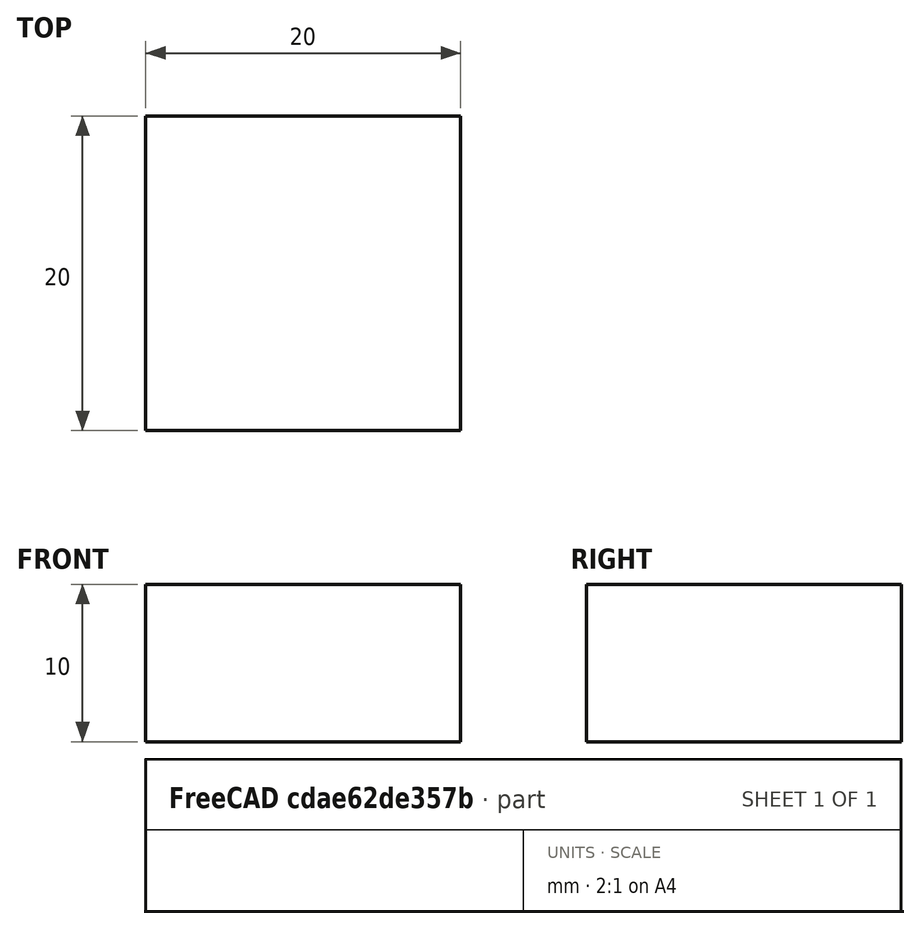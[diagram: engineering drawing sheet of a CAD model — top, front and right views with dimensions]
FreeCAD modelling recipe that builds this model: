
FCSTD DOCUMENT  (FreeCAD 1.0R39319 (Git))
Label: PD_PadWithMidplaneFC102
License: Creative Commons Attribution 4.0
LicenseURL: https://creativecommons.org/licenses/by/4.0/
objects: Sketcher::SketchObject×1, PartDesign::Pad×1, PartDesign::Body×1
note: 6 computed .brp shape members not serialized (recipe doc carries the construction recipe); baked Part::Feature solids carry a one-line shape summary decoded from their .brp

FEATURE [Sketcher::SketchObject] Sketch
  ArcFitTolerance = 1e-06
  AttachmentSupport = -> [XY_Plane]
  FullyConstrained = true
  MakeInternals = false
  MapMode = 5
  sketch-geometry (4):
    g0: LineSegment StartX=0 StartY=0 StartZ=0 EndX=20 EndY=0 EndZ=0
    g1: LineSegment StartX=20 StartY=0 StartZ=0 EndX=20 EndY=20 EndZ=0
    g2: LineSegment StartX=20 StartY=20 StartZ=0 EndX=0 EndY=20 EndZ=0
    g3: LineSegment StartX=0 StartY=20 StartZ=0 EndX=0 EndY=0 EndZ=0
  constraints (11):
    c: Coincident(g0,g1)
    c: Coincident(g1,g2)
    c: Coincident(g2,g3)
    c: Coincident(g3,g0)
    c: Horizontal(g0)
    c: Horizontal(g2)
    c: Vertical(g1)
    c: Vertical(g3)
    c: Distance(g1,g3) = 20
    c: Distance(g0,g2) = 20
    c: Coincident(g0,g-1)
FEATURE [PartDesign::Pad] Pad
  Direction = (0,0,1)
  Length = 10
  Length2 = 10
  Midplane = true
  Profile = -> Sketch
  ReferenceAxis = -> Sketch [N_Axis]
  Refine = true
  Suppressed = false
  Type = 0
FEATURE [PartDesign::Body] Body
  AllowCompound = false
  Group = -> [Sketch,Pad]
  Origin = -> Origin
  Tip = -> Pad
